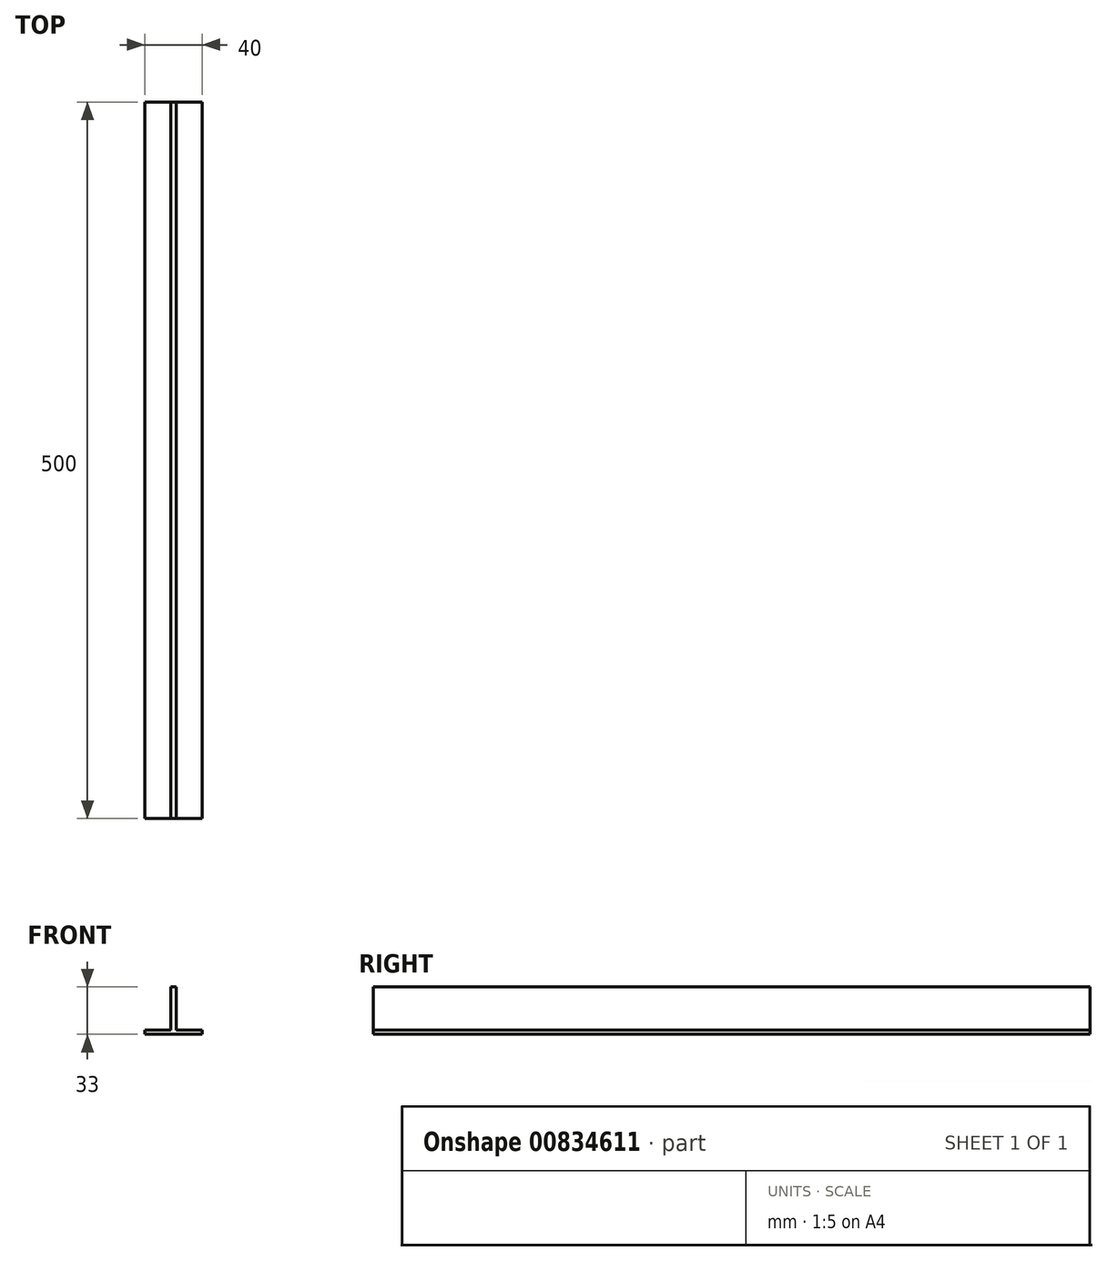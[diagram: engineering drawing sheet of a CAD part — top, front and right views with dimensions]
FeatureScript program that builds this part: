
annotation { "Feature Type Name" : "Feature", "Feature Type Description" : "" }
export const myFeature = defineFeature(function(context is Context, id is Id, definition is map)
    precondition{}
    {
        {
            var Q0;
            Q0=qCreatedBy(makeId("Front.planeOp"),FACE);
            var sketch = newSketch(context, id + "F0", { "sketchPlane" : qUnion([Q0])});
            skLineSegment(sketch, "E0.bottom", {"start": v(-20, 3) * mm, "end": v(20, 3) * mm});
            skLineSegment(sketch, "E0.top", {"start": v(-20, 0) * mm, "end": v(20, 0) * mm});
            skLineSegment(sketch, "E0.left", {"start": v(-20, 3) * mm, "end": v(-20, 0) * mm});
            skLineSegment(sketch, "E0.right", {"start": v(20, 3) * mm, "end": v(20, 0) * mm});
            skLineSegment(sketch, "E1.bottom", {"start": v(-2, 3) * mm, "end": v(2, 3) * mm});
            skLineSegment(sketch, "E1.top", {"start": v(-2, 33) * mm, "end": v(2, 33) * mm});
            skLineSegment(sketch, "E1.left", {"start": v(-2, 3) * mm, "end": v(-2, 33) * mm});
            skLineSegment(sketch, "E1.right", {"start": v(2, 3) * mm, "end": v(2, 33) * mm});
            skSolve(sketch);
        }
        {
            var Q0;
            Q0=makeQuery(id+"F0.imprint","IMPRINT",FACE,{"disambiguationData":[TD([[makeQuery(id+"F0.imprint","IMPRINT",EDGE,{"derivedFrom":sQuery(id+"F0.wireOp",EDGE,"E1.top")}),-1.0]])]});
            var Q1;
            Q1=makeQuery(id+"F0.imprint","IMPRINT",FACE,{"disambiguationData":[TD([[makeQuery(id+"F0.imprint","IMPRINT",EDGE,{"derivedFrom":sQuery(id+"F0.wireOp",EDGE,"E0.top")}),1.0]])]});
            extrude(context, id + "F1", {"entities" : qUnion([Q0, Q1]), "depth" : 500 * mm, "offsetDistance" : 25 * mm});
        }
    });
